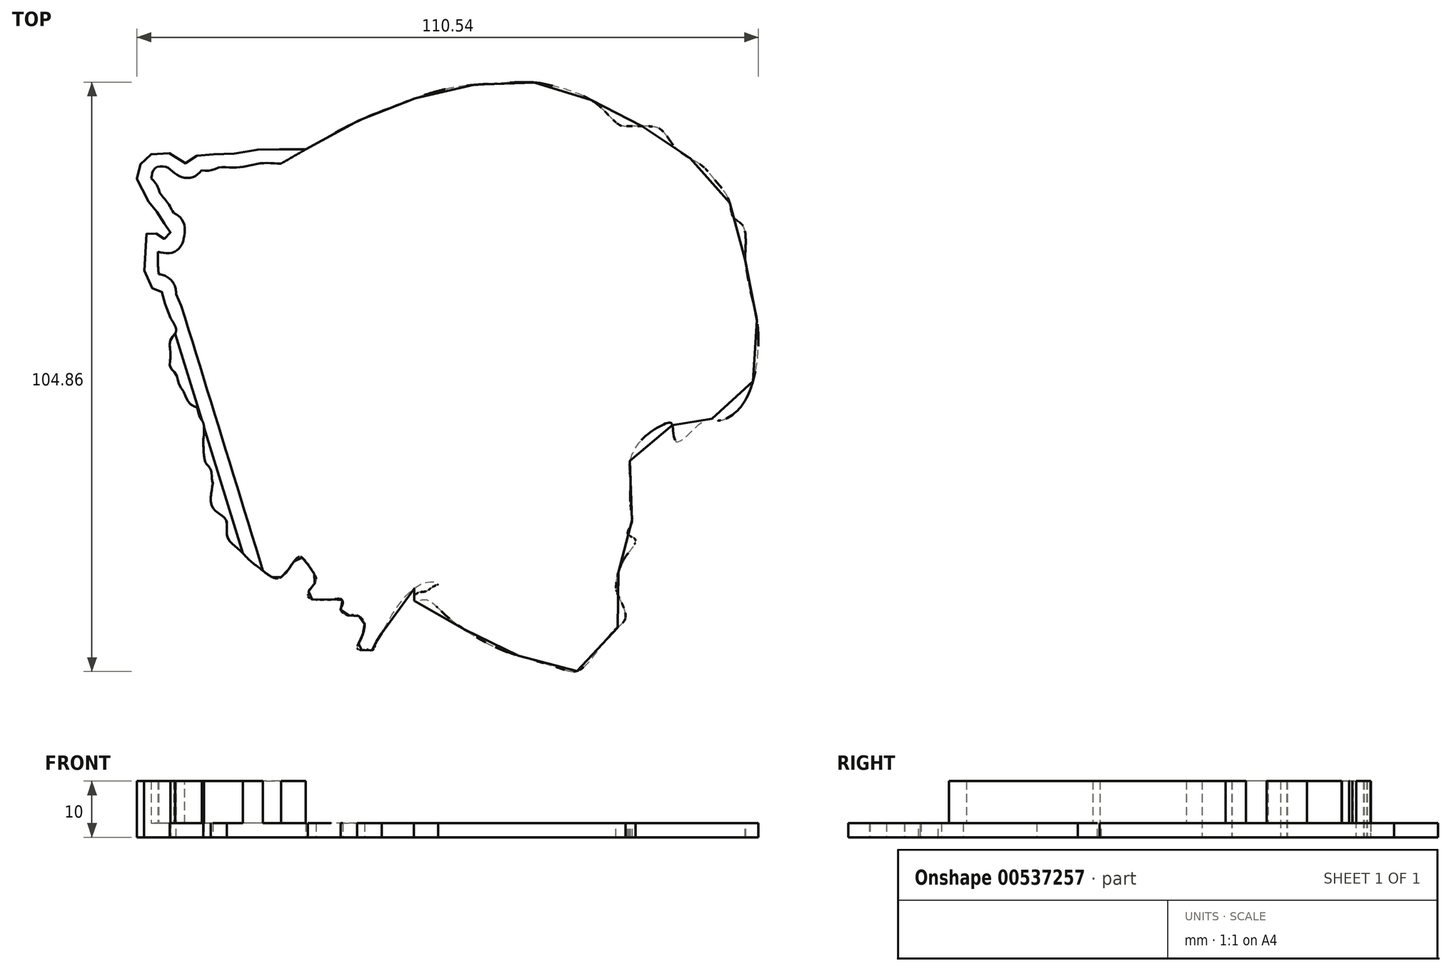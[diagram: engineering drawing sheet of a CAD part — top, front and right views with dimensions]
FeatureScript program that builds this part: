
annotation { "Feature Type Name" : "Feature", "Feature Type Description" : "" }
export const myFeature = defineFeature(function(context is Context, id is Id, definition is map)
    precondition{}
    {
        {
            var Q0;
            Q0=qCreatedBy(makeId("Top.planeOp"),FACE);
            var sketch = newSketch(context, id + "F0", { "sketchPlane" : qUnion([Q0])});
            skFitSpline(sketch, "E0", {"points": [v(-33.63, 33.97) * mm, v(-38.65, 33.97) * mm, v(-41.95, 33.97) * mm, v(-45.96, 33.25) * mm, v(-49.4, 33.25) * mm, v(-51.27, 32.68) * mm, v(-53.42, 32.68) * mm, v(-54.57, 31.39) * mm, v(-56.58, 32.68) * mm, v(-58.58, 33.4) * mm, v(-61.16, 33.1) * mm, v(-62.6, 31.96) * mm, v(-63.17, 30.96) * mm, v(-63.6, 29.1) * mm, v(-63.6, 28.23) * mm, v(-63.03, 27.23) * mm, v(-62.31, 26.37) * mm, v(-61.74, 24.94) * mm, v(-60.88, 23.79) * mm, v(-60.16, 22.93) * mm, v(-59.44, 21.64) * mm, v(-58.58, 20.63) * mm, v(-57.72, 20.06) * mm, v(-57.72, 19.06) * mm, v(-58, 18.05) * mm, v(-58.73, 18.05) * mm, v(-59.3, 18.2) * mm, v(-59.73, 18.77) * mm, v(-60.73, 19.06) * mm, v(-61.3, 19.06) * mm, v(-61.88, 19.06) * mm, v(-62.02, 10.16) * mm, v(-61.16, 9.3) * mm, v(-60.16, 9.3) * mm, v(-59.3, 8.87) * mm, v(-59.16, 7.87) * mm, v(-58.87, 7) * mm, v(-58.15, 5.29) * mm, v(-57.72, 4) * mm], "startDerivative": vector(-114.22, -1.83) * mm, "endDerivative": vector(15.34, -49.78) * mm});
            skFitSpline(sketch, "E1", {"points": [v(-57.72, 4) * mm, v(-56.72, 1.56) * mm, v(-57.72, 0) * mm, v(-57.72, -1.88) * mm, v(-57.72, -3.32) * mm, v(-57.72, -4.75) * mm, v(-56.72, -6.04) * mm, v(-56.29, -7.48) * mm, v(-55.28, -9.34) * mm, v(-54, -11.5) * mm, v(-52.85, -12.07) * mm, v(-52.7, -13.07) * mm, v(-51.84, -14.8) * mm, v(-51.84, -17.52) * mm, v(-51.84, -18.8) * mm, v(-51.41, -21.82) * mm, v(-50.55, -22.97) * mm, v(-50.26, -25.12) * mm, v(-50.12, -25.4) * mm], "startDerivative": vector(25.16, -38.37) * mm, "endDerivative": vector(6.84, -7.69) * mm});
            skFitSpline(sketch, "E2", {"points": [v(-50.12, -25.4) * mm, v(-50.12, -29.87) * mm, v(-47.84, -31.93) * mm, v(-47.6, -34.91) * mm, v(-45.54, -37.2) * mm, v(-43.48, -39.27) * mm, v(-41.42, -40.87) * mm, v(-38.2, -42.25) * mm, v(-35, -38.58) * mm, v(-33.85, -39.04) * mm, v(-32.7, -40.64) * mm, v(-31.79, -42.7) * mm, v(-32.93, -44.31) * mm, v(-33.16, -45.69) * mm, v(-32.02, -46.15) * mm, v(-30.18, -46.15) * mm, v(-29.26, -46.15) * mm, v(-27.2, -46.15) * mm, v(-27.2, -47.3) * mm, v(-27.43, -47.98) * mm, v(-26.28, -48.9) * mm, v(-24.68, -48.9) * mm, v(-23.3, -50.05) * mm, v(-23.3, -51.65) * mm, v(-24, -53.48) * mm, v(-24.45, -54.86) * mm, v(-23.53, -55.09) * mm, v(-22.39, -55.09) * mm, v(-21.7, -55.09) * mm, v(-21, -53.48) * mm, v(-20.1, -52.1) * mm], "startDerivative": vector(-20.32, -100.66) * mm, "endDerivative": vector(32.54, 38.25) * mm});
            skFitSpline(sketch, "E3", {"points": [v(-20.1, -52.1) * mm, v(-16.01, -45.7) * mm, v(-11.58, -42.96) * mm, v(-10.1, -43.38) * mm, v(-10.95, -43.8) * mm, v(-12.21, -44.65) * mm, v(-13.9, -45.07) * mm, v(-14.32, -46.34) * mm, v(-12.42, -46.13) * mm, v(-9.26, -48.45) * mm, v(-4.4, -52.1) * mm, v(1.5, -55.2) * mm, v(11, -58.16) * mm, v(15.23, -58.58) * mm, v(20.72, -52.1) * mm, v(23.25, -49.3) * mm, v(21.98, -45.5) * mm, v(21.56, -43.8) * mm, v(22.62, -39.58) * mm, v(24.52, -36.84) * mm, v(24.94, -35.36) * mm, v(23.67, -34.51) * mm, v(24.3, -32.61) * mm, v(24.3, -30.71) * mm, v(24.1, -27.76) * mm, v(24.1, -24.17) * mm, v(23.88, -22.27) * mm, v(26, -17.84) * mm, v(30.22, -14.88) * mm, v(31.48, -14.88) * mm, v(32.33, -18.05) * mm, v(37.6, -14.04) * mm, v(39.71, -14.25) * mm, v(44.15, -11.3) * mm, v(46.9, 0) * mm, v(46.05, 6.44) * mm, v(45.41, 8.97) * mm, v(45, 11.3) * mm, v(44.57, 13.83) * mm, v(44.57, 15.94) * mm, v(44.15, 20.37) * mm, v(42.46, 21.85) * mm, v(41.61, 25.02) * mm, v(39.08, 28.6) * mm, v(36.76, 31.14) * mm, v(32.33, 34.1) * mm, v(29.58, 37.47) * mm, v(26.84, 38.1) * mm, v(23.88, 38.1) * mm, v(22.2, 38.31) * mm, v(18.82, 41.48) * mm, v(15.02, 43.8) * mm, v(10.37, 45.28) * mm, v(6.57, 45.91) * mm, v(0, 45.7) * mm, v(-5.25, 45.28) * mm, v(-11.37, 44.01) * mm, v(-17.7, 41.7) * mm, v(-24.03, 39.16) * mm, v(-33.63, 33.97) * mm], "startDerivative": vector(153.72, 289.16) * mm, "endDerivative": vector(-352.35, -202.35) * mm});
            skSolve(sketch);
        }
        {
            var Q0;
            Q0=makeQuery(id+"F0.imprint","IMPRINT",FACE,{"disambiguationData":[TD([[makeQuery(id+"F0.imprint","IMPRINT",EDGE,{"derivedFrom":sQuery(id+"F0.wireOp",EDGE,"E0")}),1.0]])]});
            extrude(context, id + "F1", {"entities" : qUnion([Q0]), "depth" : 10 * mm, "offsetDistance" : 25.4 * mm});
        }
        {
            var Q0;
            Q0=makeQuery(id+"F1.opExtrude","SWEPT_FACE",FACE,{"disambiguationData":[OSD([sQuery(id+"F0.wireOp",EDGE,"E3")])]});
            var Q1;
            Q1=makeQuery(id+"F1.opExtrude","SWEPT_FACE",FACE,{"disambiguationData":[OSD([sQuery(id+"F0.wireOp",EDGE,"E2")])]});
            var Q2;
            Q2=makeQuery(id+"F1.opExtrude","SWEPT_FACE",FACE,{"disambiguationData":[OSD([sQuery(id+"F0.wireOp",EDGE,"E1")])]});
            var Q3;
            Q3=makeQuery(id+"F1.opExtrude","CAP_FACE",FACE,{"disambiguationData":[OSD([sQuery(id+"F0.wireOp",EDGE,"E0"),sQuery(id+"F0.wireOp",EDGE,"E1"),sQuery(id+"F0.wireOp",EDGE,"E2"),sQuery(id+"F0.wireOp",EDGE,"E3")])],"isStart":false});
            shell(context, id + "F2", {"entities" : qUnion([Q0, Q1, Q2, Q3]), "thickness" : 2.5 * mm});
        }
        {
            var Q0;
            Q0=makeQuery(id+"F1.opExtrude","CAP_FACE",FACE,{"disambiguationData":[OSD([sQuery(id+"F0.wireOp",EDGE,"E0"),sQuery(id+"F0.wireOp",EDGE,"E1"),sQuery(id+"F0.wireOp",EDGE,"E2"),sQuery(id+"F0.wireOp",EDGE,"E3")])],"isStart":false});
            var Q1;
            Q1=makeQuery(id+"F1.opExtrude","SWEPT_FACE",FACE,{"disambiguationData":[OSD([sQuery(id+"F0.wireOp",EDGE,"E1")])]});
            var Q2;
            Q2=makeQuery(id+"F1.opExtrude","SWEPT_FACE",FACE,{"disambiguationData":[OSD([sQuery(id+"F0.wireOp",EDGE,"E2")])]});
            var Q3;
            Q3=makeQuery(id+"F1.opExtrude","SWEPT_FACE",FACE,{"disambiguationData":[OSD([sQuery(id+"F0.wireOp",EDGE,"E3")])]});
            var Q4;
            Q4=makeQuery(id+"F1.opExtrude","SWEPT_FACE",FACE,{"disambiguationData":[OSD([sQuery(id+"F0.wireOp",EDGE,"E0")])]});
            shell(context, id + "F3", {"entities" : qUnion([Q0, Q1, Q2, Q3, Q4]), "thickness" : 2.5 * mm});
        }
    });
